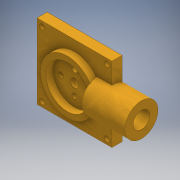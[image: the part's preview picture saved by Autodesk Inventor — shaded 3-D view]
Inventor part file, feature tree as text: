
AUTODESK INVENTOR PART (.ipt)
format: ipt  version: 2017 SP1 (Build 210196100, 196)  size: 191,488 bytes
history: native  units: mm
features: extrude x6, sketch x6
ambient origin geometry x8: Origin, YZ Plane, XZ Plane, XY Plane, X Axis, Y Axis, Z Axis, Center Point
bodies: Solid1 (feature_tree)
feature tree (12):
  extrude  "Extrusion1"  Depth=5.0mm TaperAngle=0.0deg
  extrude  "Extrusion2"  Depth=26.0mm
  extrude  "Extrusion3"  Depth=52.0mm
  extrude  "Extrusion4"  Depth=7.0mm
  extrude  "Extrusion5"  Depth=3.6mm
  extrude  "Extrusion6"  Depth=10.5mm
  sketch  "Sketch1"  dims[d0=29.6mm d1=5.0mm d2=0.0mm]
  sketch  "Sketch2"  dims[d3=26.0mm d4=26.0mm]
  sketch  "Sketch3"  dims[d5=52.0mm d6=52.0mm]
  sketch  "Sketch4"  dims[d7=7.0mm d8=0.0mm d11=3.6mm]
  sketch  "Sketch5"  dims[d12=3.6mm d13=3.6mm]
  sketch  "Sketch6"  dims[d14=3.6mm d15=6.0mm d16=15.0mm d17=0.0mm d18=1.0mm d19=11.6mm d20=19.5mm d21=10.5mm d22=0.0mm d23=0.0mm d24=32.0mm d25=0.0mm d26=22.5mm d27=22.5mm d28=45.0mm d29=45.0mm d30=3.6mm d31=3.6mm d32=3.6mm d33=3.6mm d34=32.0mm d35=0.0mm]
